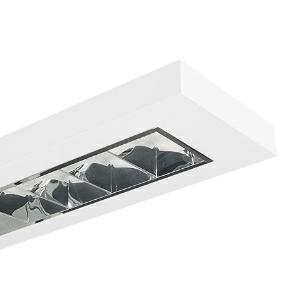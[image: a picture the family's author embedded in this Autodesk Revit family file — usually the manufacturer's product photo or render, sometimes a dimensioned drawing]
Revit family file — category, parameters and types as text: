
# Revit family: 3f_filippi_-_3f_travetta_tunable_white_2mg_3f_filippi_-_10763_-_3f_trav__led_2x22w_dali_dt8_tw_2mg_l1590__cct_6500__b26d
name_source: partatom
category: Lighting Fixtures
units: mm (PartAtom-declared; Revit-internal decimal feet)

## family parameters
Cut with Voids When Loaded = No
Host = Face
Light Source = No
Part Type = Normal
Room Calculation Point = No
Round Connector Dimension = Use Diameter
Shared = No

## types (1)
- 3F Filippi - 3F Travetta Tunable White 2MG (1 x LED, 6236 lm, 50 W, 4000 K)
    Apparent Load = 50 VA
    Approval mark = ENEC
    CIE Flux Codes = 72 99 100 100 100
    Color Rendering = 80
    Color Temperature = 4000 K
    Control Gear = Electronic transformer
    Default Elevation = 1800 mm
    Description = ILLUMINOTECHNICAL
Luminous efficiency 100% (DLOR 100%, ULOR 0%).
Luminaire luminous flux 5800 lm @ 2700 K.
Luminaire luminous flux 6236 lm @ 4000 K.
Luminaire luminous flux 6236 lm @ 6500 K.
Direct symmetric distribution.
Installation Interdistance Transv.D = 1.29 x hu - Long.D = 1.23 x hu.
Average luminance <1000 cd/m² for radial angles >65°.
Tabular UGR (CIE 117 - 4H-8H; S=0.25H; 70/50/20): RUG 17.1 - 19.3.
Beam angle: 80° - 84°.
Luminous efficacy 125 lm/W.
Lifetime (L90/B10): 30000 h. (tq+25°C)
Lifetime (L85/B10): 50000 h. (tq+25°C)
Lifetime (L75/B10): 80000 h. (tq+25°C)
Lifetime (L70/B10): 100000 h. (tq+25°C)
Sudden decreased luminous flux after 50000 hours: 0% (C0).
Photobiological safety in compliance with IEC/TR 62778: RG0 risk exempt, (IEC 62471).
In compliance with IEC/EN 62722-2-1 - IEC/EN 62717 standards.

SOURCE
2 linear LED modules 22W/TW.
Energy efficiency class (UE 2019/2020 - UE 2019/2015): D.
CIE 13.3 Colour rendering index: CRI >80 (R9 <50%).
IES TM-30 Fidelity Index: Rf = 84 Rg = 95.
The colour temperature can be adjusted between 2700 K and 6500 K.
Colour initial tolerance (MacAdam): SDCM 2.

MECHANICAL
Housing with squared shape in white painted galvannealed steel, with nonreflecting surface.
2MG parabolic louvre, high efficiency, in specular aluminium with superficial titanium-magnesium treatment, non-iridescent, with transverse blades closed at the top.
Prismatic flat diffuser in transparent methacrylate (PMMA), multilenticular, anti-glare, prismatic exterior, placed above louvre blades.
Film protective against dust and finger marks, adhesive, attached to louvre.
Luminaire with limited surface temperature. - D - (EN 60598-2-24)
Dimensions: 1590x190 mm, height 60 mm (edge 40 mm). Weight 5.35 kg.
IP20 protection degree.
Mechanical strength to impacts IK02 (0.2 joule).
Glow-wire test resistance 650°C.

ELECTRICAL
Halogen Free DALI DT8, PUSH-DIM, electronic wiring 230V-50/60Hz, power factor 0.95, THD <25%, constant output power, SELV, class I, 1 driver, 1 DALI addresse.
Power of the luminaire 50 W.
CE - IEC 60598-1 - EN 60598-1.
SAFE FLICKER: PstLM=<1 and SVM=<0.4 (IEC TR 61547-1 and IEC TR 63158), to ensure a more comfortable and safe light.
Luminaire compliant with EN 60598-2-22 for power supply from a centralised emergency system CPSS (Central Power Supply System), not incorporated in the luminaire - high risk areas excluded. The default power and flux are 100% in AC and 15% in DC.
Ambient temperature from 0°C to +25°C.
Temperature class T6 max 85°C.
5-pole terminal block (L-N-PE-DA/DA) for line connection with connection capacity 2x2.5 mm².
Relative humidity UR: <85%.

INSTALLATION
Suspended.
All accessories dedicated to this product are available on the Catalog and on our website www.3F-Filippi.com.

APPLICATIONS
Any environments requiring light which aims for the wellness of people.
In environments, even with reduced height, requiring a comfortable light. Offices with VDTs, managerial offices and staterooms.

LIGHT MANAGEMENT
Recommended minimum setting: 10%.
The luminaire, equipped with DALI DT8 driver, is designed for adjusting the luminous flux and colour temperature; can be controlled manually or automatically/manually with 3F HCL technology or 3F Bluetooth.

WARNING
Luminaire designed for disposal/recycling at end-of-life.
Replaceable (LED only) light source by a professional. Replaceable control gear by a professional.
    Height = 60 mm  [stored 0.19685 ft]
    Lamp = 1 x LED
    Lamp Light Flux = 6236 lm
    Lamp Power = 50 W
    Lamp count = 1
    Length = 1590 mm
    Lifetime = 50000 h
    Luminous efficacy = 125 lm/W
    Manufacturer = 3F Filippi
    ModVariant = No
    Model = 3F Filippi - 10763 - 3F TRAV. LED 2X22W DALI DT8 TW 2MG L1590 (CCT 6500)
    Mounting Place = Ceiling
    Mounting Type = Pendant
    Number of Poles = 1
    OnlyDefault = Yes
    Power Factor = 1
    Product Name = 3F Filippi - 3F Travetta Tunable White 2MG
    Product group = pendant luminaire
    ProductGroupID = 9
    Protection Class = Protection class I
    Protection Degree = IP 20
    RLX_Detail_Level = 1
    RLX_Emergency_Light_Flux = 0 lm
    RLX_Emergency_Type = 0
    RLX_Emergency_Type_DB = No
    RlxData = <blob elided: 56573 chars, md5=b34328ba>
    Socket = socket
    Standby Power = 0 W
    System Light Flux = 6236 lm
    System Power = 50 W
    Type Comments = Product without accessories
    Type Image = 3ffilippi_3f_travetta_led_2mg.jpg
    URL = http://relux.com
    VarID = ---
    Voltage = 0 V
    Weight = 0.00 kg
    Width = 190 mm  [stored 0.62336 ft]

note: [stored X ft] marks values corroborated as IEEE doubles in the binary element streams (Revit-internal decimal feet)

## geometry (parser evidence)
native form markers: Blend x4, Sweep x11
no freeform markers — native parametric forms only
